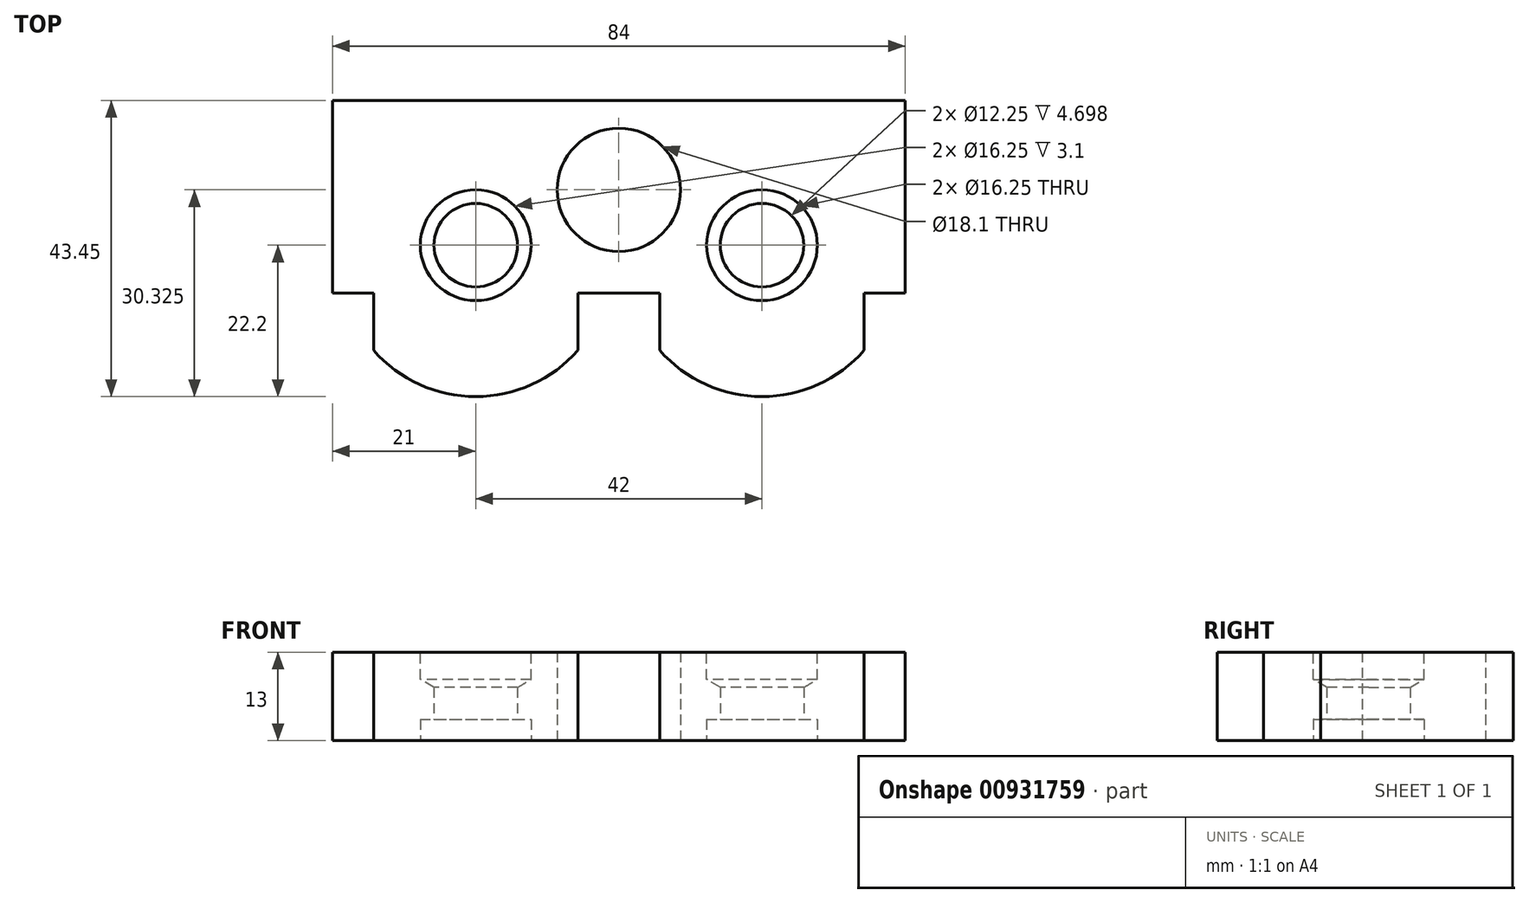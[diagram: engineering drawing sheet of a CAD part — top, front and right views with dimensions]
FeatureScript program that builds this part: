
annotation { "Feature Type Name" : "Feature", "Feature Type Description" : "" }
export const myFeature = defineFeature(function(context is Context, id is Id, definition is map)
    precondition{}
    {
        {
            var Q0;
            Q0=qCreatedBy(makeId("Top.planeOp"),FACE);
            var sketch = newSketch(context, id + "F0", { "sketchPlane" : qUnion([Q0])});
            skLineSegment(sketch, "E0", {"start": v(0, 0) * mm, "end": v(-42, 0) * mm});
            skLineSegment(sketch, "E1", {"start": v(0, 0) * mm, "end": v(42, 0) * mm});
            skLineSegment(sketch, "E2", {"start": v(-42, 0) * mm, "end": v(-42, -5) * mm});
            skLineSegment(sketch, "E3", {"start": v(-42, -5) * mm, "end": v(0, -5) * mm});
            skLineSegment(sketch, "E4", {"start": v(42, -5) * mm, "end": v(42, 0) * mm});
            skLineSegment(sketch, "E5", {"start": v(42, -5) * mm, "end": v(0, -5) * mm});
            skLineSegment(sketch, "E6", {"start": v(0, -5) * mm, "end": v(0, 0) * mm});
            skLineSegment(sketch, "E7", {"start": v(0, 0) * mm, "end": v(-21, 0) * mm});
            skLineSegment(sketch, "E8", {"start": v(-21, 0) * mm, "end": v(-21, -5) * mm});
            skLineSegment(sketch, "E9", {"start": v(0, 0) * mm, "end": v(21, 0) * mm});
            skLineSegment(sketch, "E10", {"start": v(21, 0) * mm, "end": v(21, -5) * mm});
            skLineSegment(sketch, "E11", {"start": v(-42, -5) * mm, "end": v(-42, -21.25) * mm});
            skLineSegment(sketch, "E12", {"start": v(0, -5) * mm, "end": v(0, -21.25) * mm});
            skLineSegment(sketch, "E13", {"start": v(42, -5) * mm, "end": v(42, -21.25) * mm});
            skLineSegment(sketch, "E14", {"start": v(0, -21.25) * mm, "end": v(42, -21.25) * mm});
            skLineSegment(sketch, "E15", {"start": v(-42, -21.25) * mm, "end": v(0, -21.25) * mm});
            skLineSegment(sketch, "E16", {"start": v(-21, -5) * mm, "end": v(-21, -21.25) * mm});
            skLineSegment(sketch, "E17", {"start": v(21, -5) * mm, "end": v(21, -21.25) * mm});
            skLineSegment(sketch, "E18", {"start": v(-42, -21.25) * mm, "end": v(-42, -28.25) * mm});
            skLineSegment(sketch, "E19", {"start": v(-42, -28.25) * mm, "end": v(-21, -28.25) * mm});
            skLineSegment(sketch, "E20", {"start": v(-21, -28.25) * mm, "end": v(-21, -21.25) * mm});
            skLineSegment(sketch, "E21", {"start": v(-21, -28.25) * mm, "end": v(0, -28.25) * mm});
            skLineSegment(sketch, "E22", {"start": v(0, -28.25) * mm, "end": v(0, -21.25) * mm});
            skLineSegment(sketch, "E23", {"start": v(0, -28.25) * mm, "end": v(21, -28.25) * mm});
            skLineSegment(sketch, "E24", {"start": v(21, -28.25) * mm, "end": v(21, -21.25) * mm});
            skLineSegment(sketch, "E25", {"start": v(21, -28.25) * mm, "end": v(42, -28.25) * mm});
            skLineSegment(sketch, "E26", {"start": v(42, -28.25) * mm, "end": v(42, -21.25) * mm});
            skLineSegment(sketch, "E27", {"start": v(36, -36.68) * mm, "end": v(36, -28.25) * mm});
            skLineSegment(sketch, "E28", {"start": v(36, -28.25) * mm, "end": v(42, -28.25) * mm});
            skLineSegment(sketch, "E29", {"start": v(-42, -28.25) * mm, "end": v(-36, -28.25) * mm});
            skLineSegment(sketch, "E30", {"start": v(-36, -28.25) * mm, "end": v(-36, -36.68) * mm});
            skLineSegment(sketch, "E31", {"start": v(0, -28.25) * mm, "end": v(-6, -28.25) * mm});
            skLineSegment(sketch, "E32", {"start": v(-6, -28.25) * mm, "end": v(-6, -36.68) * mm});
            skLineSegment(sketch, "E33", {"start": v(0, -28.25) * mm, "end": v(6, -28.25) * mm});
            skLineSegment(sketch, "E34", {"start": v(6, -28.25) * mm, "end": v(6, -36.68) * mm});
            skArc(sketch, "E35", {"start": v(6, -36.68) * mm, "mid": v(21, -43.45) * mm, "end": v(36, -36.68) * mm});
            skArc(sketch, "E36", {"start": v(-36, -36.68) * mm, "mid": v(-21, -43.45) * mm, "end": v(-6, -36.68) * mm});
            skPoint(sketch, "E37", {"position": v(0, -13.13) * mm});
            skLineSegment(sketch, "E38", {"start": v(-21, 0) * mm, "end": v(-26, 0) * mm});
            skLineSegment(sketch, "E39", {"start": v(21, 0) * mm, "end": v(26, 0) * mm});
            skSolve(sketch);
        }
        {
            var Q0;
            Q0 = qSketchRegion(id + "F0", true);
            var Q1;
            {var subQ0=sQuery(id+"F0.wireOp",EDGE,"E12");Q1=makeQuery(id+"F0.imprint","IMPRINT",FACE,{"disambiguationData":[TD([[makeQuery(id+"F0.imprint","IMPRINT",EDGE,{"derivedFrom":subQ0}),1.0]])]});}
            var Q2;
            {var subQ0=sQuery(id+"F0.wireOp",EDGE,"E12");Q2=makeQuery(id+"F0.imprint","IMPRINT",FACE,{"disambiguationData":[TD([[makeQuery(id+"F0.imprint","IMPRINT",EDGE,{"derivedFrom":subQ0}),-1.0]])]});}
            extrude(context, id + "F1", {"entities" : qUnion([Q0, Q1, Q2]), "depth" : 13 * mm, "offsetDistance" : 25 * mm});
        }
        {
            var Q0;
            Q0=sQuery(id+"F0.wireOp",VERTEX,"E17.end");
            var Q1;
            Q1=sQuery(id+"F0.wireOp",VERTEX,"E16.end");
            var Q2;
            Q2=makeQuery(id+"F1.opExtrude","SWEPT_BODY",BODY,{"disambiguationData":[OSD([sQuery(id+"F0.wireOp",EDGE,"E0"),sQuery(id+"F0.wireOp",EDGE,"E1"),sQuery(id+"F0.wireOp",EDGE,"E2"),sQuery(id+"F0.wireOp",EDGE,"E4"),sQuery(id+"F0.wireOp",EDGE,"E7"),sQuery(id+"F0.wireOp",EDGE,"E9"),sQuery(id+"F0.wireOp",EDGE,"E11"),sQuery(id+"F0.wireOp",EDGE,"E13"),sQuery(id+"F0.wireOp",EDGE,"E18"),sQuery(id+"F0.wireOp",EDGE,"E26"),sQuery(id+"F0.wireOp",EDGE,"E27"),sQuery(id+"F0.wireOp",EDGE,"E28"),sQuery(id+"F0.wireOp",EDGE,"E29"),sQuery(id+"F0.wireOp",EDGE,"E30"),sQuery(id+"F0.wireOp",EDGE,"E31"),sQuery(id+"F0.wireOp",EDGE,"E32"),sQuery(id+"F0.wireOp",EDGE,"E33"),sQuery(id+"F0.wireOp",EDGE,"E34"),sQuery(id+"F0.wireOp",EDGE,"E35"),sQuery(id+"F0.wireOp",EDGE,"E36")])]});
            hole(context, id + "F2", {"style" : HoleStyle.C_BORE, "endStyle" : HoleEndStyle.THROUGH, "oppositeDirection" : true, "holeDiameter" : 12.25 * mm, "cBoreDiameter" : 16.25 * mm, "cBoreDepth" : 3.1 * mm, "majorDiameter" : 5 * mm, "isTappedThrough" : true, "tappedDepth" : 12 * mm, "tapClearance" : 3, "locations" : qUnion([Q0, Q1]), "scope" : qUnion([Q2])});
        }
        {
            var Q0;
            Q0=makeQuery(id+"F1.opExtrude","CAP_FACE",FACE,{"disambiguationData":[OSD([sQuery(id+"F0.wireOp",EDGE,"E0"),sQuery(id+"F0.wireOp",EDGE,"E1"),sQuery(id+"F0.wireOp",EDGE,"E2"),sQuery(id+"F0.wireOp",EDGE,"E4"),sQuery(id+"F0.wireOp",EDGE,"E7"),sQuery(id+"F0.wireOp",EDGE,"E9"),sQuery(id+"F0.wireOp",EDGE,"E11"),sQuery(id+"F0.wireOp",EDGE,"E13"),sQuery(id+"F0.wireOp",EDGE,"E18"),sQuery(id+"F0.wireOp",EDGE,"E26"),sQuery(id+"F0.wireOp",EDGE,"E27"),sQuery(id+"F0.wireOp",EDGE,"E28"),sQuery(id+"F0.wireOp",EDGE,"E29"),sQuery(id+"F0.wireOp",EDGE,"E30"),sQuery(id+"F0.wireOp",EDGE,"E31"),sQuery(id+"F0.wireOp",EDGE,"E32"),sQuery(id+"F0.wireOp",EDGE,"E33"),sQuery(id+"F0.wireOp",EDGE,"E34"),sQuery(id+"F0.wireOp",EDGE,"E35"),sQuery(id+"F0.wireOp",EDGE,"E36")])],"isStart":false});
            var sketch = newSketch(context, id + "F3", { "sketchPlane" : qUnion([Q0])});
            skPoint(sketch, "E40", {"position": v(-21, -21.25) * mm});
            skPoint(sketch, "E41", {"position": v(21, -21.25) * mm});
            skSolve(sketch);
        }
        {
            var Q0;
            Q0=sQuery(id+"F3.wireOp",VERTEX,"E40");
            var Q1;
            Q1=sQuery(id+"F3.wireOp",VERTEX,"E41");
            var Q2;
            Q2=makeQuery(id+"F1.opExtrude","SWEPT_BODY",BODY,{"disambiguationData":[OSD([sQuery(id+"F0.wireOp",EDGE,"E0"),sQuery(id+"F0.wireOp",EDGE,"E1"),sQuery(id+"F0.wireOp",EDGE,"E2"),sQuery(id+"F0.wireOp",EDGE,"E4"),sQuery(id+"F0.wireOp",EDGE,"E7"),sQuery(id+"F0.wireOp",EDGE,"E9"),sQuery(id+"F0.wireOp",EDGE,"E11"),sQuery(id+"F0.wireOp",EDGE,"E13"),sQuery(id+"F0.wireOp",EDGE,"E18"),sQuery(id+"F0.wireOp",EDGE,"E26"),sQuery(id+"F0.wireOp",EDGE,"E27"),sQuery(id+"F0.wireOp",EDGE,"E28"),sQuery(id+"F0.wireOp",EDGE,"E29"),sQuery(id+"F0.wireOp",EDGE,"E30"),sQuery(id+"F0.wireOp",EDGE,"E31"),sQuery(id+"F0.wireOp",EDGE,"E32"),sQuery(id+"F0.wireOp",EDGE,"E33"),sQuery(id+"F0.wireOp",EDGE,"E34"),sQuery(id+"F0.wireOp",EDGE,"E35"),sQuery(id+"F0.wireOp",EDGE,"E36")])]});
            hole(context, id + "F4", {"style" : HoleStyle.SIMPLE, "endStyle" : HoleEndStyle.BLIND, "holeDiameter" : 16.25 * mm, "majorDiameter" : 5 * mm, "holeDepth" : 4 * mm, "isTappedThrough" : true, "tappedDepth" : 12 * mm, "tapClearance" : 3, "locations" : qUnion([Q0, Q1]), "scope" : qUnion([Q2])});
        }
        {
            var Q0;
            Q0=sQuery(id+"F0.wireOp",VERTEX,"E37");
            var Q1;
            Q1=makeQuery(id+"F1.opExtrude","SWEPT_BODY",BODY,{"disambiguationData":[OSD([sQuery(id+"F0.wireOp",EDGE,"E0"),sQuery(id+"F0.wireOp",EDGE,"E1"),sQuery(id+"F0.wireOp",EDGE,"E2"),sQuery(id+"F0.wireOp",EDGE,"E4"),sQuery(id+"F0.wireOp",EDGE,"E7"),sQuery(id+"F0.wireOp",EDGE,"E9"),sQuery(id+"F0.wireOp",EDGE,"E11"),sQuery(id+"F0.wireOp",EDGE,"E13"),sQuery(id+"F0.wireOp",EDGE,"E18"),sQuery(id+"F0.wireOp",EDGE,"E26"),sQuery(id+"F0.wireOp",EDGE,"E27"),sQuery(id+"F0.wireOp",EDGE,"E28"),sQuery(id+"F0.wireOp",EDGE,"E29"),sQuery(id+"F0.wireOp",EDGE,"E30"),sQuery(id+"F0.wireOp",EDGE,"E31"),sQuery(id+"F0.wireOp",EDGE,"E32"),sQuery(id+"F0.wireOp",EDGE,"E33"),sQuery(id+"F0.wireOp",EDGE,"E34"),sQuery(id+"F0.wireOp",EDGE,"E35"),sQuery(id+"F0.wireOp",EDGE,"E36")])]});
            hole(context, id + "F5", {"style" : HoleStyle.SIMPLE, "endStyle" : HoleEndStyle.THROUGH, "oppositeDirection" : true, "holeDiameter" : 18.1 * mm, "majorDiameter" : 5 * mm, "isTappedThrough" : true, "tappedDepth" : 12 * mm, "tapClearance" : 3, "locations" : qUnion([Q0]), "scope" : qUnion([Q1])});
        }
    });
